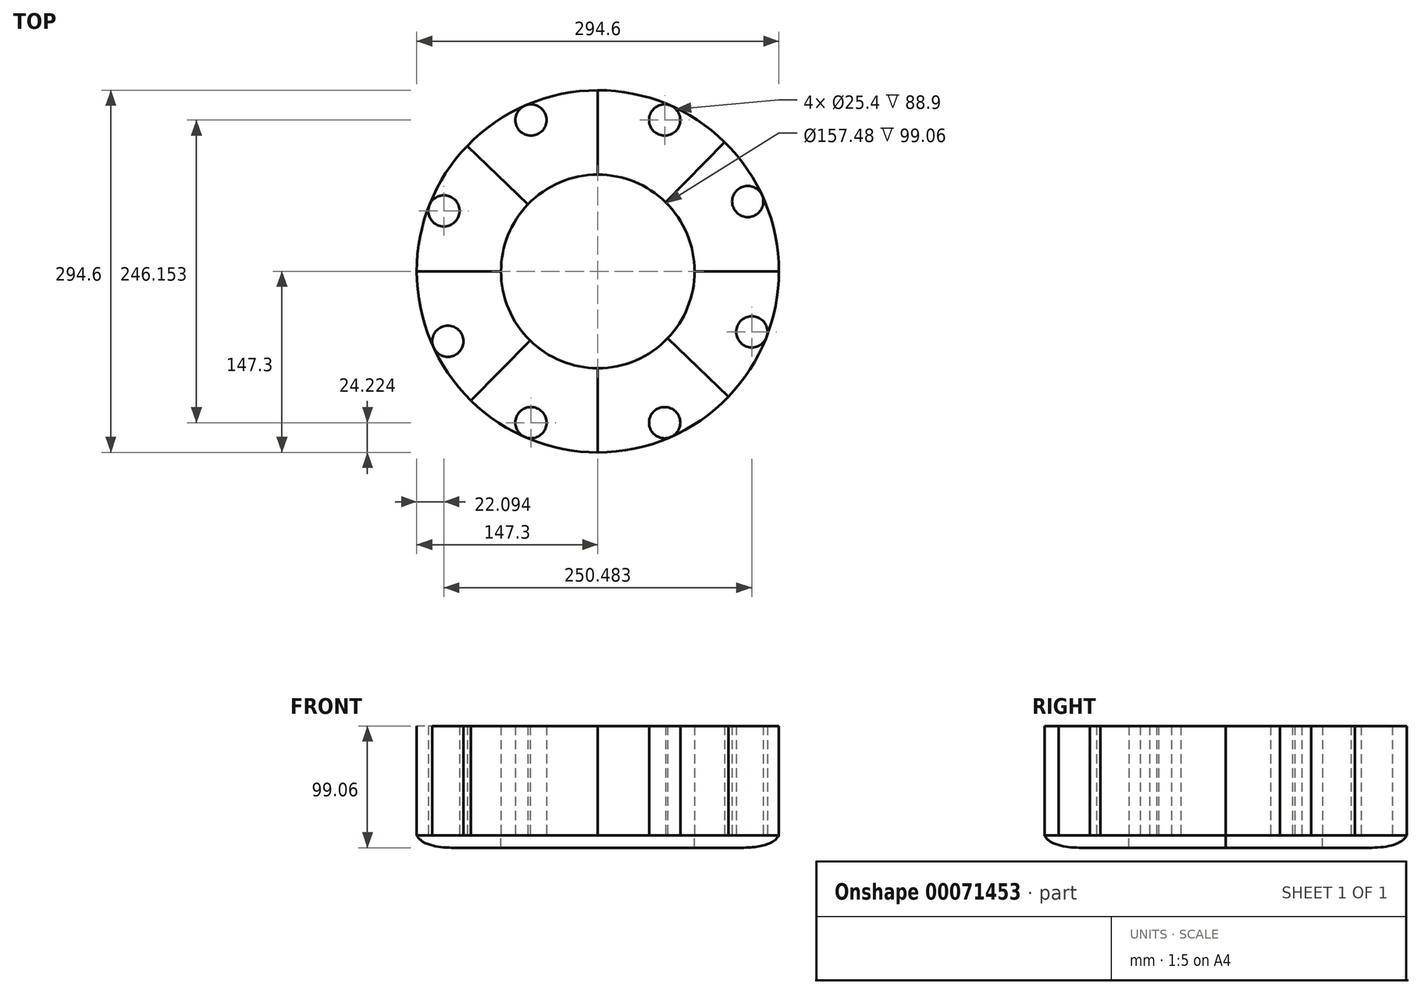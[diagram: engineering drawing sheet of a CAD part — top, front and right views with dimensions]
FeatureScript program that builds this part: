
annotation { "Feature Type Name" : "Feature", "Feature Type Description" : "" }
export const myFeature = defineFeature(function(context is Context, id is Id, definition is map)
    precondition{}
    {
        {
            var Q0;
            Q0=qCreatedBy(makeId("Front.planeOp"),FACE);
            var sketch = newSketch(context, id + "F0", { "sketchPlane" : qUnion([Q0])});
            skLineSegment(sketch, "E0", {"start": v(0, 0) * mm, "end": v(-78.74, 0) * mm});
            skLineSegment(sketch, "E1.bottom", {"start": v(-78.74, 0) * mm, "end": v(-116.84, 0) * mm});
            skLineSegment(sketch, "E1.top", {"start": v(-78.74, 10.16) * mm, "end": v(-116.84, 10.16) * mm});
            skLineSegment(sketch, "E1.left", {"start": v(-78.74, 0) * mm, "end": v(-78.74, 10.16) * mm});
            skLineSegment(sketch, "E1.right", {"start": v(-116.84, 0) * mm, "end": v(-116.84, 10.16) * mm});
            skLineSegment(sketch, "E2", {"start": v(-147.3, 10.16) * mm, "end": v(-116.84, 10.16) * mm});
            skLineSegment(sketch, "E3", {"start": v(0, 26.06) * mm, "end": v(0, 0) * mm});
            skFitSpline(sketch, "E4", {"points": [v(-147.3, 10.16) * mm, v(-116.84, 0) * mm], "startDerivative": vector(11.25, -22.77) * mm, "endDerivative": vector(44.23, 0) * mm});
            skSolve(sketch);
        }
        {
            var Q0;
            Q0=makeQuery(id+"F0.imprint","IMPRINT",FACE,{"disambiguationData":[TD([[makeQuery(id+"F0.imprint","IMPRINT",EDGE,{"derivedFrom":sQuery(id+"F0.wireOp",EDGE,"E1.right")}),1.0]])]});
            var Q1;
            Q1=makeQuery(id+"F0.imprint","IMPRINT",FACE,{"disambiguationData":[TD([[makeQuery(id+"F0.imprint","IMPRINT",EDGE,{"derivedFrom":sQuery(id+"F0.wireOp",EDGE,"E1.bottom")}),-1.0]])]});
            var Q2;
            Q2=sQuery(id+"F0.wireOp",EDGE,"E3");
            revolve(context, id + "F1", {"entities" : qUnion([Q0, Q1]), "axis" : qUnion([Q2]), "revolveType" : RevolveType.FULL});
        }
        {
            var Q0;
            Q0=makeQuery(id+"F1.opRevolve","SWEPT_FACE",FACE,{"disambiguationData":[OSD([sQuery(id+"F0.wireOp",EDGE,"E1.top"),sQuery(id+"F0.wireOp",EDGE,"E2")])]});
            var sketch = newSketch(context, id + "F2", { "sketchPlane" : qUnion([Q0])});
            skLineSegment(sketch, "E5", {"start": v(0, -147.3) * mm, "end": v(0, 147.3) * mm});
            skLineSegment(sketch, "E6", {"start": v(-147.3, 0) * mm, "end": v(147.3, 0) * mm});
            skLineSegment(sketch, "E7", {"start": v(-106.29, 101.97) * mm, "end": v(106.32, -101.94) * mm});
            skLineSegment(sketch, "E8", {"start": v(-103.12, -105.18) * mm, "end": v(103.12, 105.18) * mm});
            skCircle(sketch, "E9", {"center": v(-54.4, 123.08) * mm, "radius": 12.7 * mm});
            skCircle(sketch, "E10.MirrorC", {"center": v(54.4, 123.08) * mm, "radius": 12.7 * mm});
            skCircle(sketch, "E11.MirrorC", {"center": v(-54.4, -123.08) * mm, "radius": 12.7 * mm});
            skCircle(sketch, "E12.MirrorC", {"center": v(54.4, -123.08) * mm, "radius": 12.7 * mm});
            skCircle(sketch, "E13.MirrorC", {"center": v(-125.2, 49.24) * mm, "radius": 12.7 * mm});
            skCircle(sketch, "E14.MirrorC", {"center": v(125.28, -49.17) * mm, "radius": 12.7 * mm});
            skCircle(sketch, "E15.MirrorC", {"center": v(-121.98, -56.81) * mm, "radius": 12.7 * mm});
            skCircle(sketch, "E16.MirrorC", {"center": v(121.98, 56.81) * mm, "radius": 12.7 * mm});
            skSolve(sketch);
        }
        {
            var Q0;
            Q0=makeQuery(id+"F2.imprint","IMPRINT",FACE,{"disambiguationData":[TD([[makeQuery(id+"F2.imprint","IMPRINT",EDGE,{"derivedFrom":sQuery(id+"F2.wireOp",EDGE,"E9")}),1.0]])]});
            var Q1;
            Q1=makeQuery(id+"F2.imprint","IMPRINT",FACE,{"disambiguationData":[TD([[makeQuery(id+"F2.imprint","IMPRINT",EDGE,{"derivedFrom":sQuery(id+"F2.wireOp",EDGE,"E10.MirrorC")}),-1.0]])]});
            var Q2;
            Q2=makeQuery(id+"F2.imprint","IMPRINT",FACE,{"disambiguationData":[TD([[makeQuery(id+"F2.imprint","IMPRINT",EDGE,{"derivedFrom":sQuery(id+"F2.wireOp",EDGE,"E16.MirrorC")}),1.0]])]});
            var Q3;
            Q3=makeQuery(id+"F2.imprint","IMPRINT",FACE,{"disambiguationData":[TD([[makeQuery(id+"F2.imprint","IMPRINT",EDGE,{"derivedFrom":sQuery(id+"F2.wireOp",EDGE,"E14.MirrorC")}),-1.0]])]});
            var Q4;
            Q4=makeQuery(id+"F2.imprint","IMPRINT",FACE,{"disambiguationData":[TD([[makeQuery(id+"F2.imprint","IMPRINT",EDGE,{"derivedFrom":sQuery(id+"F2.wireOp",EDGE,"E12.MirrorC")}),1.0]])]});
            var Q5;
            Q5=makeQuery(id+"F2.imprint","IMPRINT",FACE,{"disambiguationData":[TD([[makeQuery(id+"F2.imprint","IMPRINT",EDGE,{"derivedFrom":sQuery(id+"F2.wireOp",EDGE,"E11.MirrorC")}),-1.0]])]});
            var Q6;
            Q6=makeQuery(id+"F2.imprint","IMPRINT",FACE,{"disambiguationData":[TD([[makeQuery(id+"F2.imprint","IMPRINT",EDGE,{"derivedFrom":sQuery(id+"F2.wireOp",EDGE,"E15.MirrorC")}),1.0]])]});
            var Q7;
            {var subQ0=sQuery(id+"F2.wireOp",EDGE,"E13.MirrorC");var subQ1=makeQuery(id+"F1.opRevolve","SWEPT_EDGE",EDGE,{"disambiguationData":[OSD([sQuery(id+"F0.wireOp",EDGE,"XMNss6VD-mHXe-QgiY-B8lY-crOFBOULQMyg"),sQuery(id+"F0.wireOp",EDGE,"E2")])]});var subQ2=makeQuery(id+"F2.imprint","INTERSECT",VERTEX,{"disambiguationData":[OD(0.0)],"derivedFrom":[subQ1,subQ0]});Q7=makeQuery(id+"F2.imprint","IMPRINT",FACE,{"disambiguationData":[TD([[makeQuery(id+"F2.imprint","IMPRINT",EDGE,{"disambiguationData":[TD([[subQ2,1.0]])],"derivedFrom":subQ0}),-1.0]])]});}
            extrude(context, id + "F3", {"entities" : qUnion([Q0, Q1, Q2, Q3, Q4, Q5, Q6, Q7]), "operationType" : NewBodyOperationType.ADD, "depth" : 88.9 * mm});
        }
        {
            var Q0;
            Q0=makeQuery(id+"F2.imprint","IMPRINT",FACE,{"disambiguationData":[TD([[makeQuery(id+"F2.imprint","IMPRINT",EDGE,{"derivedFrom":sQuery(id+"F2.wireOp",EDGE,"E13.MirrorC")}),-1.0]])]});
            extrude(context, id + "F4", {"entities" : qUnion([Q0]), "operationType" : NewBodyOperationType.ADD, "depth" : 88.9 * mm});
        }
    });
